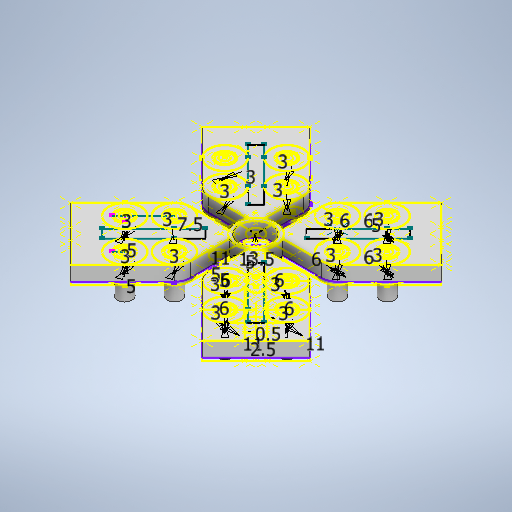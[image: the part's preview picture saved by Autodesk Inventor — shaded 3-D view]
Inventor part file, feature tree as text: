
AUTODESK INVENTOR PART (.ipt)
format: ipt  version: 2025.1 (Build 291241000, 241)  size: 1,472,000 bytes
history: native  units: in
note: dims shown in document units (in); Inventor stores cm internally (conversion verified against a paired STEP export)
features: projected_geometry x225, extrude x6, sketch x4, mirror x2
ambient origin geometry x8: Origin, YZ Plane, XZ Plane, XY Plane, X Axis, Y Axis, Z Axis, Center Point
bodies: Solid1 (feature_tree)
feature tree (237):
  sketch  "Sketch1"  dims[d0=0.1969in d1=0.5315in d2=0.1969in d3=0.0197in d4=0.0984in d5=0.1969in d6=0.4331in d7=0.4331in d8=0.1969in d9=0.1969in d10=0.4331in]
  extrude  "Extrusion1"  Depth=0.1969in
  extrude  "Extrusion2"  Depth=0.0394in TaperAngle=0.0deg
  sketch  "Sketch3"  dims[d11=0.1969in d12=0.0in d13=0.0394in d14=0.0in]
  extrude  "Extrusion3"  Depth=0.2795in TaperAngle=0.0deg
  extrude  "Extrusion4"  Depth=0.1181in
  mirror  "Mirror1"
  extrude  "Extrusion5"  Depth=0.1181in
  mirror  "Mirror2"
  extrude  "Extrusion6"  Depth=0.1181in
  sketch  "Sketch5"  dims[d18=0.1181in d19=0.1181in d20=0.1181in d21=0.1181in d22=0.1181in d23=0.1181in d24=0.1181in d25=0.1181in d26=0.1181in d27=0.1181in d28=0.1181in d29=0.1181in d30=0.1181in d31=0.1181in d32=0.1181in d33=0.1181in d34=0.2362in d35=0.2362in d36=0.2362in d37=0.2362in d38=0.0787in d39=0.0in d40=0.2362in d41=0.2362in d42=0.2362in d43=0.2362in d44=0.0787in d45=0.0in d46=0.4331in d47=0.5906in d48=0.0in d49=0.2953in]
  projected_geometry  "Projected Loop1"
  projected_geometry  "Projected Loop2"
  projected_geometry  "Projected Loop3"
  projected_geometry  "Projected Loop4"
  projected_geometry  "Projected Loop5"
  projected_geometry  "Projected Loop6"
  projected_geometry  "Projected Loop7"
  projected_geometry  "Projected Loop8"
  projected_geometry  "Projected Loop9"
  projected_geometry  "Projected Loop10"
  projected_geometry  "Projected Loop11"
  projected_geometry  "Projected Loop12"
  projected_geometry  "Projected Loop13"
  projected_geometry  "Projected Loop14"
  projected_geometry  "Projected Loop15"
  projected_geometry  "Projected Loop16"
  projected_geometry  "Projected Loop17"
  projected_geometry  "Projected Loop18"
  projected_geometry  "Projected Loop19"
  projected_geometry  "Projected Loop20"
  projected_geometry  "Projected Loop21"
  projected_geometry  "Projected Loop22"
  projected_geometry  "Projected Loop23"
  projected_geometry  "Projected Loop24"
  projected_geometry  "Projected Loop25"
  projected_geometry  "Projected Loop26"
  projected_geometry  "Projected Loop27"
  projected_geometry  "Projected Loop28"
  projected_geometry  "Projected Loop29"
  projected_geometry  "Projected Loop30"
  projected_geometry  "Projected Loop31"
  projected_geometry  "Projected Loop32"
  projected_geometry  "Projected Loop33"
  projected_geometry  "Projected Loop34"
  projected_geometry  "Projected Loop35"
  projected_geometry  "Projected Loop36"
  projected_geometry  "Projected Loop37"
  projected_geometry  "Projected Loop38"
  projected_geometry  "Projected Loop39"
  projected_geometry  "Projected Loop40"
  projected_geometry  "Projected Loop41"
  projected_geometry  "Projected Loop42"
  projected_geometry  "Projected Loop43"
  projected_geometry  "Projected Loop44"
  projected_geometry  "Projected Loop45"
  projected_geometry  "Projected Loop46"
  projected_geometry  "Projected Loop47"
  projected_geometry  "Projected Loop48"
  projected_geometry  "Projected Loop49"
  projected_geometry  "Projected Loop50"
  projected_geometry  "Projected Loop51"
  projected_geometry  "Projected Loop52"
  projected_geometry  "Projected Loop53"
  projected_geometry  "Projected Loop54"
  projected_geometry  "Projected Loop55"
  projected_geometry  "Projected Loop56"
  projected_geometry  "Projected Loop57"
  projected_geometry  "Projected Loop58"
  projected_geometry  "Projected Loop59"
  projected_geometry  "Projected Loop60"
  sketch  "Sketch4"  dims[d15=0.1969in d16=0.2795in d17=0.0in]
  projected_geometry  "Projected Loop61"
  projected_geometry  "Projected Loop62"
  projected_geometry  "Projected Loop63"
  projected_geometry  "Projected Loop64"
  projected_geometry  "Projected Loop65"
  projected_geometry  "Projected Loop66"
  projected_geometry  "Projected Loop67"
  projected_geometry  "Projected Loop68"
  projected_geometry  "Projected Loop69"
  projected_geometry  "Projected Loop70"
  projected_geometry  "Projected Loop71"
  projected_geometry  "Projected Loop72"
  projected_geometry  "Projected Loop73"
  projected_geometry  "Projected Loop74"
  projected_geometry  "Projected Loop75"
  projected_geometry  "Projected Loop76"
  projected_geometry  "Projected Loop77"
  projected_geometry  "Projected Loop78"
  projected_geometry  "Projected Loop79"
  projected_geometry  "Projected Loop80"
  projected_geometry  "Projected Loop81"
  projected_geometry  "Projected Loop82"
  projected_geometry  "Projected Loop83"
  projected_geometry  "Projected Loop84"
  projected_geometry  "Projected Loop85"
  projected_geometry  "Projected Loop86"
  projected_geometry  "Projected Loop87"
  projected_geometry  "Projected Loop88"
  projected_geometry  "Projected Loop89"
  projected_geometry  "Projected Loop90"
  projected_geometry  "Projected Loop91"
  projected_geometry  "Projected Loop92"
  projected_geometry  "Projected Loop93"
  projected_geometry  "Projected Loop94"
  projected_geometry  "Projected Loop95"
  projected_geometry  "Projected Loop96"
  projected_geometry  "Projected Loop97"
  projected_geometry  "Projected Loop98"
  projected_geometry  "Projected Loop99"
  projected_geometry  "Projected Loop100"
  projected_geometry  "Projected Loop101"
  projected_geometry  "Projected Loop102"
  projected_geometry  "Projected Loop103"
  projected_geometry  "Projected Loop104"
  projected_geometry  "Projected Loop105"
  projected_geometry  "Projected Loop106"
  projected_geometry  "Projected Loop107"
  projected_geometry  "Projected Loop108"
  projected_geometry  "Projected Loop109"
  projected_geometry  "Projected Loop110"
  projected_geometry  "Projected Loop111"
  projected_geometry  "Projected Loop112"
  projected_geometry  "Projected Loop113"
  projected_geometry  "Projected Loop114"
  projected_geometry  "Projected Loop115"
  projected_geometry  "Projected Loop116"
  projected_geometry  "Projected Loop117"
  projected_geometry  "Projected Loop118"
  projected_geometry  "Projected Loop119"
  projected_geometry  "Projected Loop120"
  projected_geometry  "Projected Loop121"
  projected_geometry  "Projected Loop122"
  projected_geometry  "Projected Loop123"
  projected_geometry  "Projected Loop124"
  projected_geometry  "Projected Loop125"
  projected_geometry  "Projected Loop126"
  projected_geometry  "Projected Loop127"
  projected_geometry  "Projected Loop128"
  projected_geometry  "Projected Loop129"
  projected_geometry  "Projected Loop130"
  projected_geometry  "Projected Loop131"
  projected_geometry  "Projected Loop132"
  projected_geometry  "Projected Loop133"
  projected_geometry  "Projected Loop134"
  projected_geometry  "Projected Loop135"
  projected_geometry  "Projected Loop136"
  projected_geometry  "Projected Loop137"
  projected_geometry  "Projected Loop138"
  projected_geometry  "Projected Loop139"
  projected_geometry  "Projected Loop140"
  projected_geometry  "Projected Loop141"
  projected_geometry  "Projected Loop142"
  projected_geometry  "Projected Loop143"
  projected_geometry  "Projected Loop144"
  projected_geometry  "Projected Loop145"
  projected_geometry  "Projected Loop146"
  projected_geometry  "Projected Loop147"
  projected_geometry  "Projected Loop148"
  projected_geometry  "Projected Loop149"
  projected_geometry  "Projected Loop150"
  projected_geometry  "Projected Loop151"
  projected_geometry  "Projected Loop152"
  projected_geometry  "Projected Loop153"
  projected_geometry  "Projected Loop154"
  projected_geometry  "Projected Loop155"
  projected_geometry  "Projected Loop156"
  projected_geometry  "Projected Loop157"
  projected_geometry  "Projected Loop158"
  projected_geometry  "Projected Loop159"
  projected_geometry  "Projected Loop160"
  projected_geometry  "Projected Loop161"
  projected_geometry  "Projected Loop162"
  projected_geometry  "Projected Loop163"
  projected_geometry  "Projected Loop164"
  projected_geometry  "Projected Loop165"
  projected_geometry  "Projected Loop166"
  projected_geometry  "Projected Loop167"
  projected_geometry  "Projected Loop168"
  projected_geometry  "Projected Loop169"
  projected_geometry  "Projected Loop170"
  projected_geometry  "Projected Loop171"
  projected_geometry  "Projected Loop172"
  projected_geometry  "Projected Loop173"
  projected_geometry  "Projected Loop174"
  projected_geometry  "Projected Loop175"
  projected_geometry  "Projected Loop176"
  projected_geometry  "Projected Loop177"
  projected_geometry  "Projected Loop178"
  projected_geometry  "Projected Loop179"
  projected_geometry  "Projected Loop180"
  projected_geometry  "Projected Loop181"
  projected_geometry  "Projected Loop182"
  projected_geometry  "Projected Loop183"
  projected_geometry  "Projected Loop184"
  projected_geometry  "Projected Loop185"
  projected_geometry  "Projected Loop186"
  projected_geometry  "Projected Loop187"
  projected_geometry  "Projected Loop188"
  projected_geometry  "Projected Loop189"
  projected_geometry  "Projected Loop190"
  projected_geometry  "Projected Loop191"
  projected_geometry  "Projected Loop192"
  projected_geometry  "Projected Loop193"
  projected_geometry  "Projected Loop194"
  projected_geometry  "Projected Loop195"
  projected_geometry  "Projected Loop196"
  projected_geometry  "Projected Loop197"
  projected_geometry  "Projected Loop198"
  projected_geometry  "Projected Loop199"
  projected_geometry  "Projected Loop200"
  projected_geometry  "Projected Loop201"
  projected_geometry  "Projected Loop202"
  projected_geometry  "Projected Loop203"
  projected_geometry  "Projected Loop204"
  projected_geometry  "Projected Loop205"
  projected_geometry  "Projected Loop206"
  projected_geometry  "Projected Loop207"
  projected_geometry  "Projected Loop208"
  projected_geometry  "Projected Loop209"
  projected_geometry  "Projected Loop210"
  projected_geometry  "Projected Loop211"
  projected_geometry  "Projected Loop212"
  projected_geometry  "Projected Loop213"
  projected_geometry  "Projected Loop214"
  projected_geometry  "Projected Loop215"
  projected_geometry  "Projected Loop216"
  projected_geometry  "Projected Loop217"
  projected_geometry  "Projected Loop218"
  projected_geometry  "Projected Loop219"
  projected_geometry  "Projected Loop220"
  projected_geometry  "Projected Loop221"
  projected_geometry  "Projected Loop222"
  projected_geometry  "Projected Loop223"
  projected_geometry  "Projected Loop224"
  projected_geometry  "Projected Loop225"
